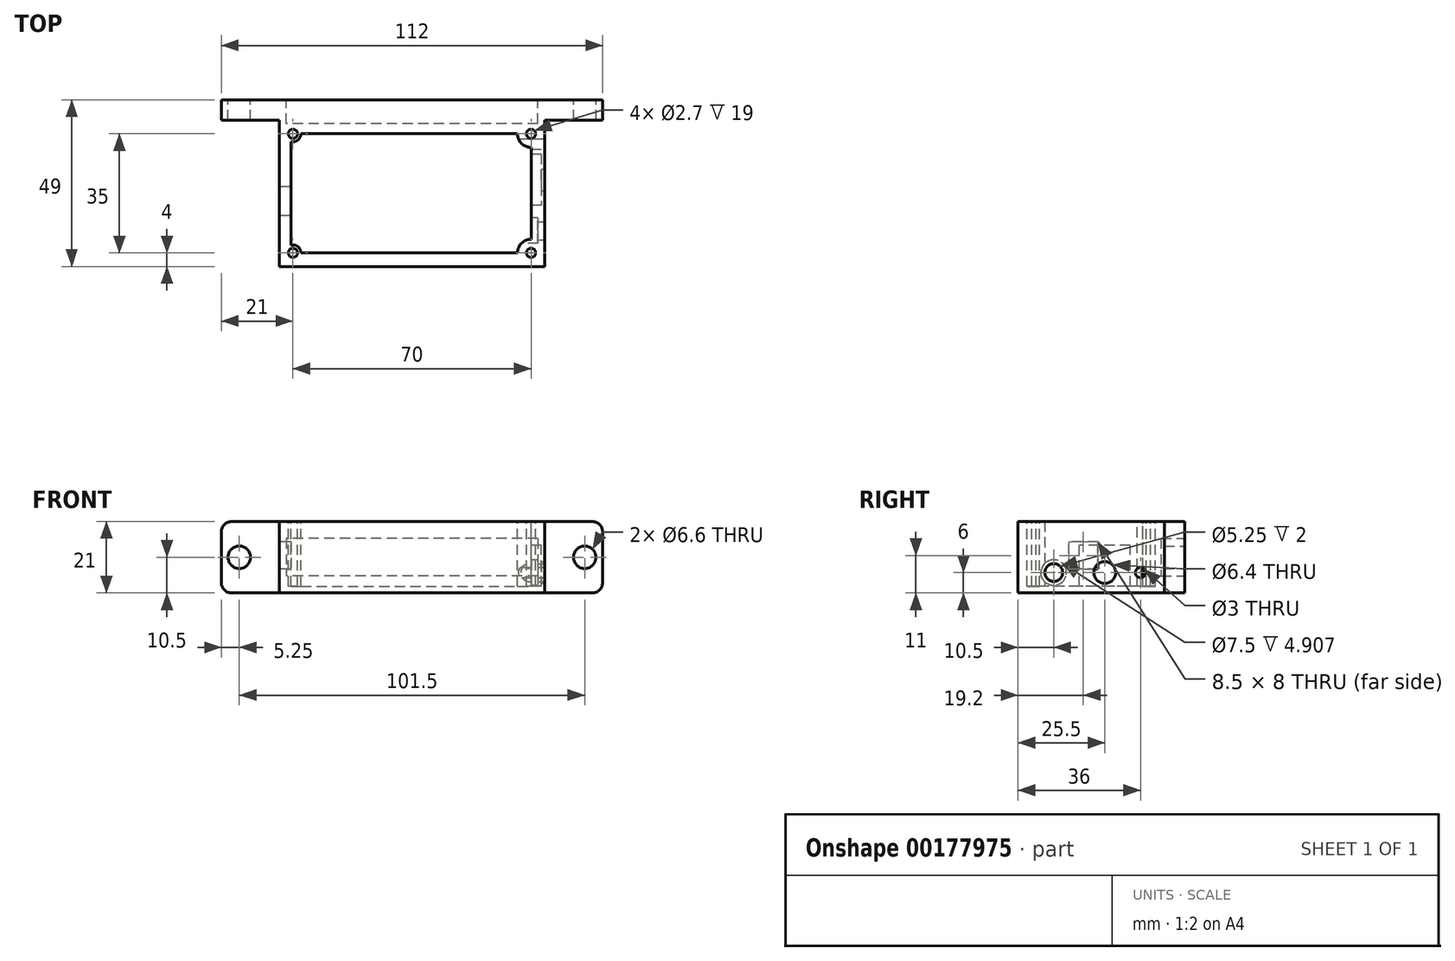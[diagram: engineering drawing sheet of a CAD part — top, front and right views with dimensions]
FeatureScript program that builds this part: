
annotation { "Feature Type Name" : "Feature", "Feature Type Description" : "" }
export const myFeature = defineFeature(function(context is Context, id is Id, definition is map)
    precondition{}
    {
        {
            var Q0;
            Q0=qCreatedBy(makeId("Top.planeOp"),FACE);
            var sketch = newSketch(context, id + "F0", { "sketchPlane" : qUnion([Q0])});
            skLineSegment(sketch, "E0.bottom", {"start": v(-39, 21.5) * mm, "end": v(39, 21.5) * mm});
            skLineSegment(sketch, "E0.top", {"start": v(-39, -21.5) * mm, "end": v(39, -21.5) * mm});
            skLineSegment(sketch, "E0.left", {"start": v(-39, 21.5) * mm, "end": v(-39, -21.5) * mm});
            skLineSegment(sketch, "E0.right", {"start": v(39, 21.5) * mm, "end": v(39, -21.5) * mm});
            skSolve(sketch);
        }
        {
            var Q0;
            Q0=qSketchRegion(id+"F0",true);
            extrude(context, id + "F1", {"entities" : qUnion([Q0]), "depth" : 21 * mm});
        }
        {
            var Q0;
            Q0=makeQuery(id+"F1.opExtrude","CAP_FACE",FACE,{"disambiguationData":[OSD([sQuery(id+"F0.wireOp",EDGE,"E0.bottom"),sQuery(id+"F0.wireOp",EDGE,"E0.top"),sQuery(id+"F0.wireOp",EDGE,"E0.left"),sQuery(id+"F0.wireOp",EDGE,"E0.right")])],"isStart":false});
            var sketch = newSketch(context, id + "F2", { "sketchPlane" : qUnion([Q0])});
            skLineSegment(sketch, "E1.1", {"start": v(-31, 17.5) * mm, "end": v(31, 17.5) * mm});
            skLineSegment(sketch, "E1.2", {"start": v(35, 13.5) * mm, "end": v(35, -13.5) * mm});
            skLineSegment(sketch, "E1.3", {"start": v(-31, -17.5) * mm, "end": v(31, -17.5) * mm});
            skArc(sketch, "E2", {"start": v(31, 17.5) * mm, "mid": v(32.17, 14.67) * mm, "end": v(35, 13.5) * mm});
            skArc(sketch, "E3", {"start": v(35, -13.5) * mm, "mid": v(32.17, -14.67) * mm, "end": v(31, -17.5) * mm});
            skCircle(sketch, "E4", {"center": v(-35, 17.5) * mm, "radius": 1.35 * mm});
            skCircle(sketch, "E5", {"center": v(35, 17.5) * mm, "radius": 1.35 * mm});
            skCircle(sketch, "E6", {"center": v(-35, -17.5) * mm, "radius": 1.35 * mm});
            skCircle(sketch, "E7", {"center": v(35, -17.5) * mm, "radius": 1.35 * mm});
            skLineSegment(sketch, "E8", {"start": v(-31, 17.5) * mm, "end": v(-31, -17.5) * mm});
            skSolve(sketch);
        }
        {
            var Q0;
            Q0=qSketchRegion(id+"F2",true);
            extrude(context, id + "F3", {"entities" : qUnion([Q0]), "operationType" : NewBodyOperationType.REMOVE, "oppositeDirection" : true, "depth" : 19 * mm});
        }
        {
            var Q0;
            Q0=makeQuery(id+"F1.opExtrude","CAP_FACE",FACE,{"disambiguationData":[OSD([sQuery(id+"F0.wireOp",EDGE,"E0.bottom"),sQuery(id+"F0.wireOp",EDGE,"E0.top"),sQuery(id+"F0.wireOp",EDGE,"E0.left"),sQuery(id+"F0.wireOp",EDGE,"E0.right")])],"isStart":false});
            var sketch = newSketch(context, id + "F4", { "sketchPlane" : qUnion([Q0])});
            skArc(sketch, "E9.0", {"start": v(-35.5, 15.2) * mm, "mid": v(-33.53, 15.67) * mm, "end": v(-32.65, 17.5) * mm});
            skLineSegment(sketch, "E10", {"start": v(-31, 17.5) * mm, "end": v(-32.65, 17.5) * mm});
            skLineSegment(sketch, "E11", {"start": v(-35.5, 15.2) * mm, "end": v(-35.5, -15.2) * mm});
            skArc(sketch, "E12.0", {"start": v(-32.65, -17.5) * mm, "mid": v(-33.53, -15.67) * mm, "end": v(-35.5, -15.2) * mm});
            skLineSegment(sketch, "E13", {"start": v(-31, -17.5) * mm, "end": v(-32.65, -17.5) * mm});
            skLineSegment(sketch, "E14", {"start": v(-31, -17.5) * mm, "end": v(-31, 17.5) * mm});
            skSolve(sketch);
        }
        {
            var Q0;
            Q0=qSketchRegion(id+"F4",true);
            extrude(context, id + "F5", {"entities" : qUnion([Q0]), "operationType" : NewBodyOperationType.REMOVE, "oppositeDirection" : true, "depth" : 19 * mm});
        }
        {
            var Q0;
            Q0=makeQuery(id+"F3.boolean.opBoolean","COPY",FACE,{"derivedFrom":makeQuery(id+"F3.opExtrude","CAP_FACE",FACE,{"disambiguationData":[OSD([sQuery(id+"F2.wireOp",EDGE,"E1.1"),sQuery(id+"F2.wireOp",EDGE,"E1.2"),sQuery(id+"F2.wireOp",EDGE,"E1.3"),sQuery(id+"F2.wireOp",EDGE,"E2"),sQuery(id+"F2.wireOp",EDGE,"E3"),sQuery(id+"F2.wireOp",EDGE,"E8")])],"isStart":false})});
            var sketch = newSketch(context, id + "F6", { "sketchPlane" : qUnion([Q0])});
            skLineSegment(sketch, "E15.bottom", {"start": v(35, 10.5) * mm, "end": v(21.5, 10.5) * mm, "construction": true});
            skLineSegment(sketch, "E15.top", {"start": v(35, -2.5) * mm, "end": v(21.5, -2.5) * mm, "construction": true});
            skLineSegment(sketch, "E15.left", {"start": v(35, 10.5) * mm, "end": v(35, -2.5) * mm, "construction": true});
            skLineSegment(sketch, "E15.right", {"start": v(21.5, 10.5) * mm, "end": v(21.5, -2.5) * mm, "construction": true});
            skLineSegment(sketch, "E16.bottom", {"start": v(-10.48, -8.77) * mm, "end": v(10.52, -8.77) * mm, "construction": true});
            skLineSegment(sketch, "E16.top", {"start": v(-10.48, -15.27) * mm, "end": v(10.52, -15.27) * mm, "construction": true});
            skLineSegment(sketch, "E16.left", {"start": v(-10.48, -8.77) * mm, "end": v(-10.48, -15.27) * mm, "construction": true});
            skLineSegment(sketch, "E16.right", {"start": v(10.52, -8.77) * mm, "end": v(10.52, -15.27) * mm, "construction": true});
            skSolve(sketch);
        }
        {
            var Q0;
            Q0=makeQuery(id+"F1.opExtrude","SWEPT_FACE",FACE,{"disambiguationData":[OSD([sQuery(id+"F0.wireOp",EDGE,"E0.right")])]});
            var sketch = newSketch(context, id + "F7", { "sketchPlane" : qUnion([Q0])});
            skCircle(sketch, "E17", {"center": v(4, 6) * mm, "radius": 3.2 * mm});
            skCircle(sketch, "E18", {"center": v(14.5, 6) * mm, "radius": 1.5 * mm});
            skLineSegment(sketch, "E19", {"start": v(-25.27, 6) * mm, "end": v(30.9, 6) * mm, "construction": true});
            skCircle(sketch, "E20", {"center": v(-11, 6) * mm, "radius": 2.62 * mm});
            skSolve(sketch);
        }
        {
            var Q0;
            Q0=qSketchRegion(id+"F7",true);
            extrude(context, id + "F8", {"entities" : qUnion([Q0]), "operationType" : NewBodyOperationType.REMOVE, "oppositeDirection" : true, "depth" : 10 * mm});
        }
        {
            var Q0;
            Q0=makeQuery(id+"F1.opExtrude","SWEPT_FACE",FACE,{"disambiguationData":[OSD([sQuery(id+"F0.wireOp",EDGE,"E0.bottom")])]});
            var sketch = newSketch(context, id + "F9", { "sketchPlane" : qUnion([Q0])});
            skLineSegment(sketch, "E21.bottom", {"start": v(56, 0) * mm, "end": v(-56, 0) * mm});
            skLineSegment(sketch, "E21.top", {"start": v(56, 21) * mm, "end": v(-56, 21) * mm});
            skLineSegment(sketch, "E21.left", {"start": v(56, 0) * mm, "end": v(56, 21) * mm});
            skLineSegment(sketch, "E21.right", {"start": v(-56, 0) * mm, "end": v(-56, 21) * mm});
            skSolve(sketch);
        }
        {
            var Q0;
            Q0=qSketchRegion(id+"F9",true);
            extrude(context, id + "F10", {"entities" : qUnion([Q0]), "operationType" : NewBodyOperationType.ADD, "depth" : 6 * mm});
        }
        {
            var Q0;
            Q0=makeQuery(id+"F10.opExtrude","CAP_FACE",FACE,{"disambiguationData":[OSD([sQuery(id+"F9.wireOp",EDGE,"E21.bottom"),sQuery(id+"F9.wireOp",EDGE,"E21.top"),sQuery(id+"F9.wireOp",EDGE,"E21.left"),sQuery(id+"F9.wireOp",EDGE,"E21.right")])],"isStart":false});
            var sketch = newSketch(context, id + "F11", { "sketchPlane" : qUnion([Q0])});
            skLineSegment(sketch, "E22", {"start": v(47.23, 10.5) * mm, "end": v(-48.21, 10.5) * mm, "construction": true});
            skPoint(sketch, "E22.startSnap0", {"position": v(56, 10.5) * mm});
            skCircle(sketch, "E23", {"center": v(50.75, 10.5) * mm, "radius": 3.3 * mm});
            skCircle(sketch, "E24", {"center": v(-50.75, 10.5) * mm, "radius": 3.3 * mm});
            skSolve(sketch);
        }
        {
            var Q0;
            Q0=qSketchRegion(id+"F11",true);
            extrude(context, id + "F12", {"entities" : qUnion([Q0]), "operationType" : NewBodyOperationType.REMOVE, "endBound" : BoundingType.THROUGH_ALL, "oppositeDirection" : true, "depth" : 25 * mm});
        }
        {
            var Q0;
            Q0=makeQuery(id+"F10.opExtrude","SWEPT_EDGE",EDGE,{"disambiguationData":[OSD([sQuery(id+"F9.wireOp",EDGE,"E21.top"),sQuery(id+"F9.wireOp",EDGE,"E21.right")])]});
            var Q1;
            Q1=makeQuery(id+"F10.opExtrude","SWEPT_EDGE",EDGE,{"disambiguationData":[OSD([sQuery(id+"F9.wireOp",EDGE,"E21.bottom"),sQuery(id+"F9.wireOp",EDGE,"E21.right")])]});
            var Q2;
            Q2=makeQuery(id+"F10.opExtrude","SWEPT_EDGE",EDGE,{"disambiguationData":[OSD([sQuery(id+"F9.wireOp",EDGE,"E21.bottom"),sQuery(id+"F9.wireOp",EDGE,"E21.left")])]});
            var Q3;
            Q3=makeQuery(id+"F10.opExtrude","SWEPT_EDGE",EDGE,{"disambiguationData":[OSD([sQuery(id+"F9.wireOp",EDGE,"E21.top"),sQuery(id+"F9.wireOp",EDGE,"E21.left")])]});
            fillet(context, id + "F13", {"entities" : qUnion([Q0, Q1, Q2, Q3]), "radius" : 3 * mm, "tangentPropagation" : true, "allowEdgeOverflow" : false});
        }
        {
            var Q0;
            Q0=makeQuery(id+"F3.boolean.opBoolean","COPY",FACE,{"derivedFrom":makeQuery(id+"F3.opExtrude","SWEPT_FACE",FACE,{"disambiguationData":[OSD([sQuery(id+"F2.wireOp",EDGE,"E1.2")])]})});
            var sketch = newSketch(context, id + "F14", { "sketchPlane" : qUnion([Q0])});
            skLineSegment(sketch, "E25.bottom", {"start": v(-11.5, 2) * mm, "end": v(3.5, 2) * mm});
            skLineSegment(sketch, "E25.top", {"start": v(-11.5, 14) * mm, "end": v(3.5, 14) * mm});
            skLineSegment(sketch, "E25.left", {"start": v(-11.5, 2) * mm, "end": v(-11.5, 14) * mm});
            skLineSegment(sketch, "E25.right", {"start": v(3.5, 2) * mm, "end": v(3.5, 14) * mm});
            skLineSegment(sketch, "E26", {"start": v(-4, 19.71) * mm, "end": v(-4, -2.98) * mm, "construction": true});
            skSolve(sketch);
        }
        {
            var Q0;
            Q0=qSketchRegion(id+"F14",true);
            extrude(context, id + "F15", {"entities" : qUnion([Q0]), "operationType" : NewBodyOperationType.REMOVE, "oppositeDirection" : true, "depth" : 3 * mm});
        }
        {
            var Q0;
            Q0=makeQuery(id+"F10.opExtrude","CAP_FACE",FACE,{"disambiguationData":[OSD([sQuery(id+"F9.wireOp",EDGE,"E21.bottom"),sQuery(id+"F9.wireOp",EDGE,"E21.top"),sQuery(id+"F9.wireOp",EDGE,"E21.left"),sQuery(id+"F9.wireOp",EDGE,"E21.right")])],"isStart":false});
            var sketch = newSketch(context, id + "F16", { "sketchPlane" : qUnion([Q0])});
            skLineSegment(sketch, "E27.bottom", {"start": v(-37, 16) * mm, "end": v(37, 16) * mm});
            skLineSegment(sketch, "E27.top", {"start": v(-37, 5) * mm, "end": v(37, 5) * mm});
            skLineSegment(sketch, "E27.left", {"start": v(-37, 16) * mm, "end": v(-37, 5) * mm});
            skLineSegment(sketch, "E27.right", {"start": v(37, 16) * mm, "end": v(37, 5) * mm});
            skLineSegment(sketch, "E28", {"start": v(-47.87, 10.5) * mm, "end": v(51.75, 10.5) * mm, "construction": true});
            skPoint(sketch, "E28.startSnap0", {"position": v(-56, 10.5) * mm});
            skPoint(sketch, "E28.endSnap0", {"position": v(56, 10.5) * mm});
            skSolve(sketch);
        }
        {
            var Q0;
            Q0=qSketchRegion(id+"F16",true);
            extrude(context, id + "F17", {"entities" : qUnion([Q0]), "operationType" : NewBodyOperationType.REMOVE, "oppositeDirection" : true, "depth" : 7 * mm});
        }
        {
            var Q0;
            Q0=makeQuery(id+"F3.boolean.opBoolean","COPY",FACE,{"derivedFrom":makeQuery(id+"F3.opExtrude","SWEPT_FACE",FACE,{"disambiguationData":[OSD([sQuery(id+"F2.wireOp",EDGE,"E1.2")])]})});
            cPlane(context, id + "F18", {"entities" : qUnion([Q0]), "cplaneType" : CPlaneType.OFFSET, "offset" : 5 * mm, "width" : 150 * mm, "height" : 150 * mm});
        }
        {
            var Q0;
            Q0=qCreatedBy(id+"F18.planeOp",FACE);
            var sketch = newSketch(context, id + "F19", { "sketchPlane" : qUnion([Q0])});
            skCircle(sketch, "E29", {"center": v(11, 6) * mm, "radius": 3.75 * mm});
            skSolve(sketch);
        }
        {
            var Q0;
            Q0 = qSketchRegion(id + "F19", true);
            extrude(context, id + "F20", {"entities" : qUnion([Q0]), "operationType" : NewBodyOperationType.REMOVE, "oppositeDirection" : true, "depth" : 7 * mm});
        }
        {
            var Q0;
            Q0=makeQuery(id+"F6.imprint","IMPRINT",FACE,{"disambiguationData":[TD([[makeQuery(id+"F6.imprint","IMPRINT",EDGE,{"derivedFrom":makeQuery(id+"F3.boolean.opBoolean","COPY",EDGE,{"derivedFrom":makeQuery(id+"F3.opExtrude","CAP_EDGE",EDGE,{"disambiguationData":[OSD([sQuery(id+"F2.wireOp",EDGE,"E1.2")])],"isStart":false})})}),-1.0]])]});
            var sketch = newSketch(context, id + "F21", { "sketchPlane" : qUnion([Q0])});
            skLineSegment(sketch, "E30.bottom", {"start": v(-35.5, 14.75) * mm, "end": v(19.5, 14.75) * mm, "construction": true});
            skLineSegment(sketch, "E30.top", {"start": v(-35.5, -14.75) * mm, "end": v(19.5, -14.75) * mm, "construction": true});
            skLineSegment(sketch, "E30.left", {"start": v(-35.5, 14.75) * mm, "end": v(-35.5, -14.75) * mm, "construction": true});
            skLineSegment(sketch, "E30.right", {"start": v(19.5, 14.75) * mm, "end": v(19.5, -14.75) * mm, "construction": true});
            skSolve(sketch);
        }
        {
            var Q0;
            Q0=makeQuery(id+"F1.opExtrude","SWEPT_FACE",FACE,{"disambiguationData":[OSD([sQuery(id+"F0.wireOp",EDGE,"E0.left")])]});
            var sketch = newSketch(context, id + "F22", { "sketchPlane" : qUnion([Q0])});
            skLineSegment(sketch, "E31.bottom", {"start": v(-1.95, 7) * mm, "end": v(6.55, 7) * mm});
            skLineSegment(sketch, "E31.top", {"start": v(-1.95, 15) * mm, "end": v(6.55, 15) * mm});
            skLineSegment(sketch, "E31.left", {"start": v(-1.95, 7) * mm, "end": v(-1.95, 15) * mm});
            skLineSegment(sketch, "E31.right", {"start": v(6.55, 7) * mm, "end": v(6.55, 15) * mm});
            skSolve(sketch);
        }
        {
            var Q0;
            Q0 = qSketchRegion(id + "F22", true);
            extrude(context, id + "F23", {"entities" : qUnion([Q0]), "operationType" : NewBodyOperationType.REMOVE, "endBound" : BoundingType.UP_TO_NEXT, "oppositeDirection" : true, "depth" : 25 * mm});
        }
    });
